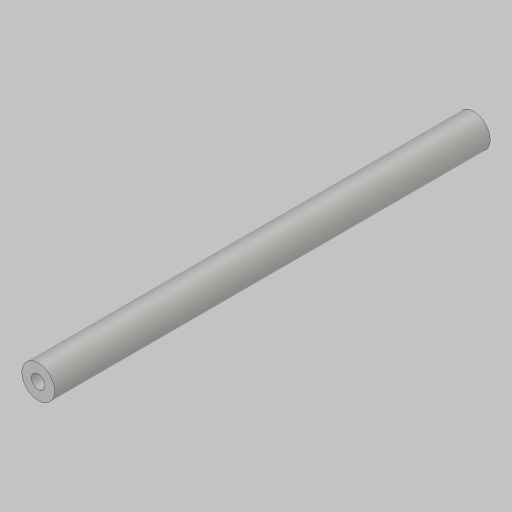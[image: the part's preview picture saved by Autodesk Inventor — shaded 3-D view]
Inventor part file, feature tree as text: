
AUTODESK INVENTOR PART (.ipt)
format: ipt  version: 2023.5 (Build 275446000, 446)  size: 101,888 bytes
history: native  units: in
note: dims shown in document units (in); Inventor stores cm internally (conversion verified against a paired STEP export)
features: extrude x1, hole x1
ambient origin geometry x8: Origin, YZ Plane, XZ Plane, XY Plane, X Axis, Y Axis, Z Axis, Center Point
bodies: Solid1 (feature_tree)
feature tree (2):
  extrude  "Extrusion1"  Depth=5.0in
  hole  "Hole1"  [1 undecoded]
note: 1 required parameter value undecoded (feature->parameter linkage not recoverable at this tier; creation-order binding heuristic only, values carry confidence <= 0.55)
